# Revit family: 01_Lavamanos 60
name_source: partatom
category: Modelos genéricos
units: mm (PartAtom-declared; Revit-internal decimal feet)

## family parameters
Compartido = No
Corte con vacíos al cargar = No
Cota de conector redondo = Diámetro de uso
Puede alojar armadura = No
Punto de cálculo de habitación = No
Se basa en plano de trabajo = No
Siempre vertical = Sí
Tipo de pieza = Normal

## types (1)
- 610x460x170
    Altura = 17 cm
    Altura a Piso = 84 cm
    Ancho = 61 cm
    Ceramico = Lavamanos Ceramico
    Comentarios de tipo = Desagüe y Sifón incluidos
    Creado por = Unibim
    Descripción = Lavamanos ceramico 610x460x170
    Elevación por defecto = 0 cm
    Especificación Técnica = LAVAMANOS 610x460x170
    Fabricante = Vatti
    Instalación = Empotrado
    Largo = 46 cm
    Material = Lavamanos Ceramico
    Modelo = Lavamanos ceramico 610x460x170
    Tamaño del producto = 610x460x170
    URL = www.vatti.cl
    _Desagüe y Sifón incluidos = Si
    _Descripción = Lavamanos ceramico
    _Fabricante = Vatti
    _Instalación = Empotrado
    _Modelo = Lavamanos ceramico 610x460x170
    _Tamaño del producto = 610x460x170
    _URL = www.vatti.cl

## geometry (parser evidence)
native form markers: Sweep x3
no freeform markers — native parametric forms only
